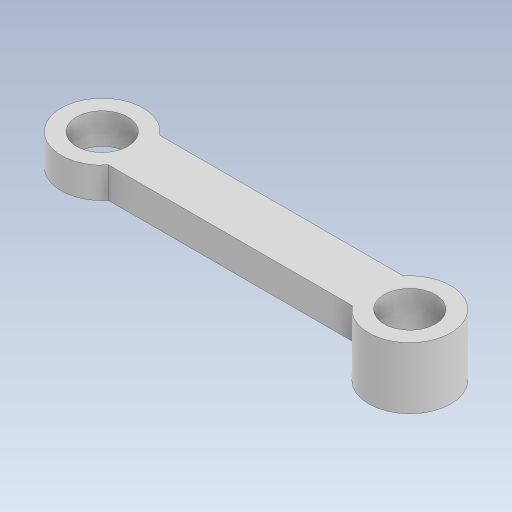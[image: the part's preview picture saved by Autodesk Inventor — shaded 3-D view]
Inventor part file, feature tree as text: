
AUTODESK INVENTOR PART (.ipt)
format: ipt  version: 2023.5 (Build 275446000, 446)  size: 279,040 bytes
history: native  units: mm
features: extrude x2, sketch x1
ambient origin geometry x8: Origin, YZ Plane, XZ Plane, XY Plane, X Axis, Y Axis, Z Axis, Center Point
bodies: Solid1 (feature_tree)
feature tree (3):
  sketch  "Sketch1"  dims[d0=5.0mm d1=8.0mm d2=5.0mm d3=8.0mm d4=30.0mm d5=3.0mm d6=0.0mm d7=3.0mm d8=0.0mm]
  extrude  "Extrusion1"  Depth=3.0mm
  extrude  "Extrusion2"  Depth=5.0mm
